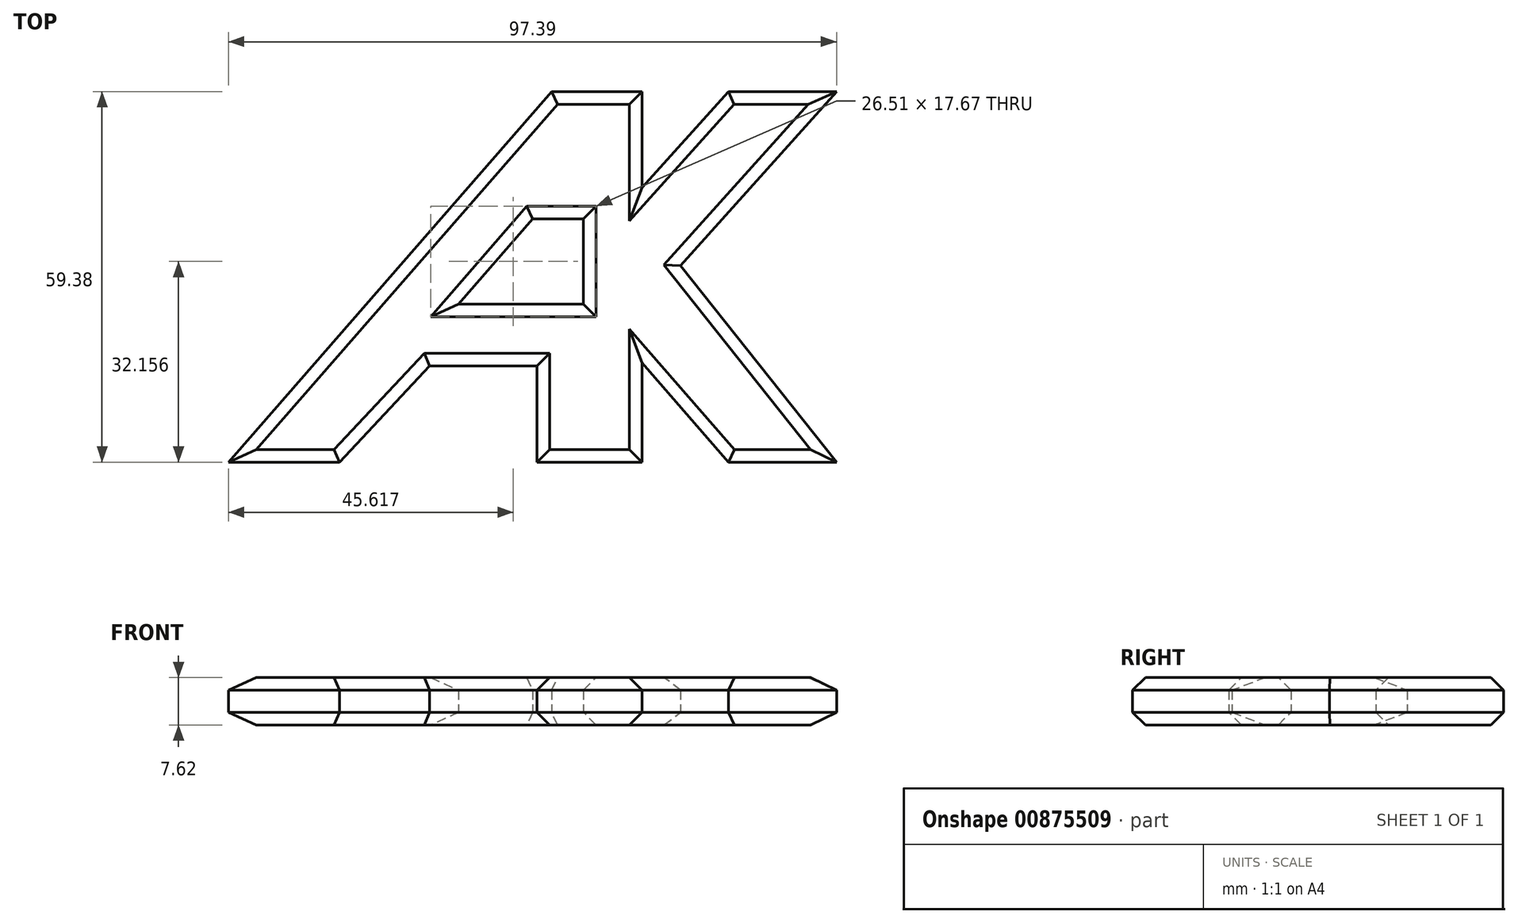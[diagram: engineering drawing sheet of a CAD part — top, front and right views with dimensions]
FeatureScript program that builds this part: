
annotation { "Feature Type Name" : "Feature", "Feature Type Description" : "" }
export const myFeature = defineFeature(function(context is Context, id is Id, definition is map)
    precondition{}
    {
        {
            var Q0;
            Q0=qCreatedBy(makeId("Top.planeOp"),FACE);
            var sketch = newSketch(context, id + "F0", { "sketchPlane" : qUnion([Q0])});
            skLineSegment(sketch, "E0", {"start": v(0, 0) * mm, "end": v(13.12, 0) * mm});
            skLineSegment(sketch, "E1", {"start": v(32.54, 15.4) * mm, "end": v(44.77, 15.4) * mm});
            skLineSegment(sketch, "E2", {"start": v(44.77, 15.4) * mm, "end": v(44.77, 0) * mm});
            skLineSegment(sketch, "E3", {"start": v(44.77, 0) * mm, "end": v(58.34, 0) * mm});
            skLineSegment(sketch, "E4", {"start": v(77.9, 0) * mm, "end": v(92.74, 0) * mm});
            skLineSegment(sketch, "E5", {"start": v(92.74, 0) * mm, "end": v(67.76, 31.5) * mm});
            skLineSegment(sketch, "E6", {"start": v(67.76, 31.5) * mm, "end": v(92.74, 59.38) * mm});
            skLineSegment(sketch, "E7", {"start": v(92.74, 59.38) * mm, "end": v(78.08, 59.38) * mm});
            skLineSegment(sketch, "E8", {"start": v(-4.65, 0) * mm, "end": v(0, 0) * mm});
            skLineSegment(sketch, "E9", {"start": v(58.34, 59.38) * mm, "end": v(47.12, 59.38) * mm});
            skLineSegment(sketch, "E10", {"start": v(47.12, 59.38) * mm, "end": v(-4.65, 0) * mm});
            skLineSegment(sketch, "E11", {"start": v(13.12, 0) * mm, "end": v(27.57, 15.4) * mm});
            skLineSegment(sketch, "E12", {"start": v(27.57, 15.4) * mm, "end": v(32.54, 15.4) * mm});
            skLineSegment(sketch, "E13", {"start": v(77.9, 0) * mm, "end": v(75.45, 0) * mm});
            skPoint(sketch, "E14.orphan", {"position": v(58.34, 22.46) * mm});
            skLineSegment(sketch, "E15", {"start": v(58.34, 0) * mm, "end": v(61.6, 0) * mm});
            skLineSegment(sketch, "E16", {"start": v(61.6, 0) * mm, "end": v(61.6, 13.1) * mm});
            skLineSegment(sketch, "E17", {"start": v(61.6, 44) * mm, "end": v(61.6, 59.38) * mm});
            skLineSegment(sketch, "E18", {"start": v(61.6, 59.38) * mm, "end": v(58.34, 59.38) * mm});
            skPoint(sketch, "E19.end.orphan", {"position": v(58.34, 43.74) * mm});
            skLineSegment(sketch, "E20", {"start": v(61.6, 44) * mm, "end": v(75.4, 59.38) * mm});
            skLineSegment(sketch, "E21", {"start": v(75.4, 59.38) * mm, "end": v(78.08, 59.38) * mm});
            skPoint(sketch, "E22.orphan", {"position": v(61.6, 41) * mm});
            skLineSegment(sketch, "E23", {"start": v(75.45, 0) * mm, "end": v(61.6, 15.9) * mm});
            skLineSegment(sketch, "E24", {"start": v(61.6, 15.9) * mm, "end": v(61.6, 13.1) * mm});
            skPoint(sketch, "E25.orphan", {"position": v(73, 0) * mm});
            skLineSegment(sketch, "E26", {"start": v(48.3, 38.96) * mm, "end": v(52.19, 38.96) * mm});
            skLineSegment(sketch, "E27", {"start": v(52.19, 38.96) * mm, "end": v(52.19, 25.35) * mm});
            skLineSegment(sketch, "E28", {"start": v(52.19, 25.35) * mm, "end": v(36.44, 25.35) * mm});
            skLineSegment(sketch, "E29", {"start": v(48.3, 38.96) * mm, "end": v(44.04, 38.96) * mm});
            skLineSegment(sketch, "E30", {"start": v(44.04, 38.96) * mm, "end": v(32.18, 25.35) * mm});
            skLineSegment(sketch, "E31", {"start": v(32.18, 25.35) * mm, "end": v(36.44, 25.35) * mm});
            skSolve(sketch);
        }
        {
            var Q0;
            Q0 = qSketchRegion(id + "F0", true);
            extrude(context, id + "F1", {"entities" : qUnion([Q0]), "depth" : 7.62 * mm, "offsetDistance" : 25.4 * mm});
        }
        {
            var Q0;
            Q0=makeQuery(id+"F1.opExtrude","CAP_FACE",FACE,{"disambiguationData":[OSD([sQuery(id+"F0.wireOp",EDGE,"E0"),sQuery(id+"F0.wireOp",EDGE,"E1"),sQuery(id+"F0.wireOp",EDGE,"E2"),sQuery(id+"F0.wireOp",EDGE,"E3"),sQuery(id+"F0.wireOp",EDGE,"E4"),sQuery(id+"F0.wireOp",EDGE,"E5"),sQuery(id+"F0.wireOp",EDGE,"E6"),sQuery(id+"F0.wireOp",EDGE,"E7"),sQuery(id+"F0.wireOp",EDGE,"E8"),sQuery(id+"F0.wireOp",EDGE,"E9"),sQuery(id+"F0.wireOp",EDGE,"E10"),sQuery(id+"F0.wireOp",EDGE,"E11"),sQuery(id+"F0.wireOp",EDGE,"E12"),sQuery(id+"F0.wireOp",EDGE,"E13"),sQuery(id+"F0.wireOp",EDGE,"E15"),sQuery(id+"F0.wireOp",EDGE,"E16"),sQuery(id+"F0.wireOp",EDGE,"E17"),sQuery(id+"F0.wireOp",EDGE,"E18"),sQuery(id+"F0.wireOp",EDGE,"E20"),sQuery(id+"F0.wireOp",EDGE,"E21"),sQuery(id+"F0.wireOp",EDGE,"E23"),sQuery(id+"F0.wireOp",EDGE,"E24"),sQuery(id+"F0.wireOp",EDGE,"E26"),sQuery(id+"F0.wireOp",EDGE,"E27"),sQuery(id+"F0.wireOp",EDGE,"E28"),sQuery(id+"F0.wireOp",EDGE,"E29"),sQuery(id+"F0.wireOp",EDGE,"E30"),sQuery(id+"F0.wireOp",EDGE,"E31")])],"isStart":false});
            var Q1;
            Q1=makeQuery(id+"F1.opExtrude","CAP_FACE",FACE,{"disambiguationData":[OSD([sQuery(id+"F0.wireOp",EDGE,"E0"),sQuery(id+"F0.wireOp",EDGE,"E1"),sQuery(id+"F0.wireOp",EDGE,"E2"),sQuery(id+"F0.wireOp",EDGE,"E3"),sQuery(id+"F0.wireOp",EDGE,"E4"),sQuery(id+"F0.wireOp",EDGE,"E5"),sQuery(id+"F0.wireOp",EDGE,"E6"),sQuery(id+"F0.wireOp",EDGE,"E7"),sQuery(id+"F0.wireOp",EDGE,"E8"),sQuery(id+"F0.wireOp",EDGE,"E9"),sQuery(id+"F0.wireOp",EDGE,"E10"),sQuery(id+"F0.wireOp",EDGE,"E11"),sQuery(id+"F0.wireOp",EDGE,"E12"),sQuery(id+"F0.wireOp",EDGE,"E13"),sQuery(id+"F0.wireOp",EDGE,"E15"),sQuery(id+"F0.wireOp",EDGE,"E16"),sQuery(id+"F0.wireOp",EDGE,"E17"),sQuery(id+"F0.wireOp",EDGE,"E18"),sQuery(id+"F0.wireOp",EDGE,"E20"),sQuery(id+"F0.wireOp",EDGE,"E21"),sQuery(id+"F0.wireOp",EDGE,"E23"),sQuery(id+"F0.wireOp",EDGE,"E24"),sQuery(id+"F0.wireOp",EDGE,"E26"),sQuery(id+"F0.wireOp",EDGE,"E27"),sQuery(id+"F0.wireOp",EDGE,"E28"),sQuery(id+"F0.wireOp",EDGE,"E29"),sQuery(id+"F0.wireOp",EDGE,"E30"),sQuery(id+"F0.wireOp",EDGE,"E31")])],"isStart":true});
            chamfer(context, id + "F2", {"entities" : qUnion([Q0, Q1]), "width" : 2.03 * mm, "tangentPropagation" : true});
        }
    });
